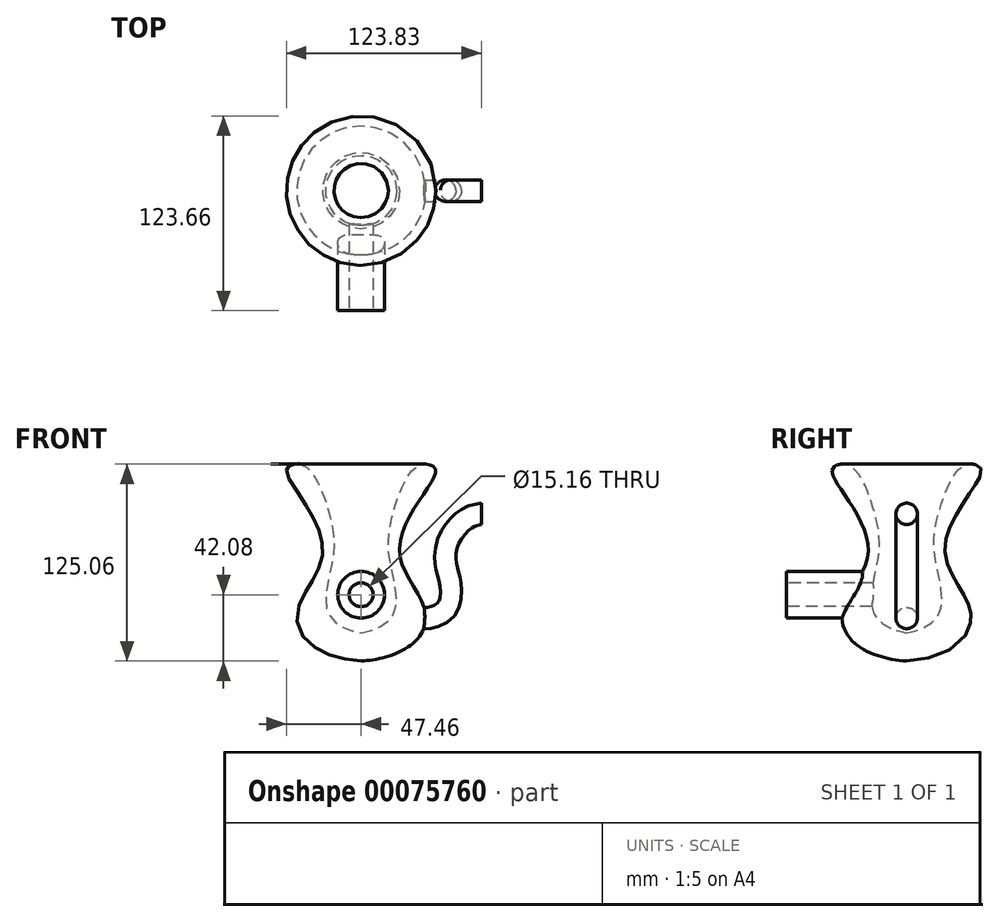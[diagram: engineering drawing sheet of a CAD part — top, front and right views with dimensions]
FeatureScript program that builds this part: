
annotation { "Feature Type Name" : "Feature", "Feature Type Description" : "" }
export const myFeature = defineFeature(function(context is Context, id is Id, definition is map)
    precondition{}
    {
        {
            var Q0;
            Q0=qCreatedBy(makeId("Front.planeOp"),FACE);
            var sketch = newSketch(context, id + "F0", { "sketchPlane" : qUnion([Q0])});
            skLineSegment(sketch, "E0", {"start": v(0, 92.1) * mm, "end": v(0, -59.81) * mm});
            skFitSpline(sketch, "E1", {"points": [v(0, -24.13) * mm, v(19.84, -13.55) * mm, v(21.5, 6.14) * mm, v(17.27, 30.67) * mm, v(19.81, 49.85) * mm, v(24.32, 64.23) * mm, v(36.45, 82) * mm, v(46.94, 80.49) * mm, v(41.13, 66.1) * mm, v(24.42, 26.34) * mm, v(40.37, -9.36) * mm, v(31.4, -32.1) * mm, v(0, -42.08) * mm, v(-7.08, -41.48) * mm, v(-6.29, -41.08) * mm, v(-12.27, -24.72) * mm], "startDerivative": vector(353.76, 54.94) * mm, "endDerivative": vector(-162.88, 343.94) * mm});
            skSolve(sketch);
        }
        {
            var Q0;
            {var subQ0=sQuery(id+"F0.wireOp",EDGE,"E1");Q0=makeQuery(id+"F0.imprint","IMPRINT",FACE,{"disambiguationData":[TD([[makeQuery(id+"F0.imprint","IMPRINT",EDGE,{"derivedFrom":subQ0}),-1.0]])]});}
            var Q1;
            Q1=sQuery(id+"F0.wireOp",EDGE,"E0");
            revolve(context, id + "F1", {"entities" : qUnion([Q0]), "axis" : qUnion([Q1]), "revolveType" : RevolveType.FULL});
        }
        {
            var Q0;
            Q0=qCreatedBy(makeId("Front.planeOp"),FACE);
            cPlane(context, id + "F2", {"entities" : qUnion([Q0]), "cplaneType" : CPlaneType.OFFSET, "offset" : 76.2 * mm, "width" : 152.4 * mm, "height" : 152.4 * mm});
        }
        {
            var Q0;
            Q0=qCreatedBy(id+"F2.planeOp",FACE);
            var sketch = newSketch(context, id + "F3", { "sketchPlane" : qUnion([Q0])});
            skCircle(sketch, "E2", {"center": v(0, 0) * mm, "radius": 14.85 * mm});
            skSolve(sketch);
        }
        {
            var Q0;
            Q0=makeQuery(id+"F3.imprint","IMPRINT",FACE,{"disambiguationData":[TD([[makeQuery(id+"F3.imprint","IMPRINT",EDGE,{"derivedFrom":sQuery(id+"F3.wireOp",EDGE,"E2")}),1.0]])]});
            var Q1;
            Q1=makeQuery(id+"F1.opRevolve","SWEPT_FACE",FACE,{"disambiguationData":[OSD([sQuery(id+"F0.wireOp",EDGE,"E1")])]});
            extrude(context, id + "F4", {"entities" : qUnion([Q0]), "operationType" : NewBodyOperationType.ADD, "endBound" : BoundingType.UP_TO_NEXT, "oppositeDirection" : true, "endBoundEntityFace" : qUnion([Q1]), "depth" : 25.4 * mm});
        }
        {
            var Q0;
            Q0=makeQuery(id+"F4.opExtrude","CAP_FACE",FACE,{"disambiguationData":[OSD([sQuery(id+"F3.wireOp",EDGE,"E2")])],"isStart":true});
            var sketch = newSketch(context, id + "F5", { "sketchPlane" : qUnion([Q0])});
            skCircle(sketch, "E3", {"center": v(0, 0) * mm, "radius": 7.58 * mm});
            skSolve(sketch);
        }
        {
            var Q0;
            Q0=makeQuery(id+"F5.imprint","IMPRINT",FACE,{"disambiguationData":[TD([[makeQuery(id+"F5.imprint","IMPRINT",EDGE,{"derivedFrom":sQuery(id+"F5.wireOp",EDGE,"E3")}),1.0]])]});
            extrude(context, id + "F6", {"entities" : qUnion([Q0]), "operationType" : NewBodyOperationType.REMOVE, "oppositeDirection" : true, "depth" : 73.26 * mm});
        }
        {
            var Q0;
            Q0=qCreatedBy(makeId("Right.planeOp"),FACE);
            cPlane(context, id + "F7", {"entities" : qUnion([Q0]), "cplaneType" : CPlaneType.OFFSET, "offset" : 76.2 * mm, "width" : 152.4 * mm, "height" : 152.4 * mm});
        }
        {
            var Q0;
            Q0=qCreatedBy(id+"F7.planeOp",FACE);
            var sketch = newSketch(context, id + "F8", { "sketchPlane" : qUnion([Q0])});
            skCircle(sketch, "E4", {"center": v(0, 51.38) * mm, "radius": 6.8 * mm});
            skSolve(sketch);
        }
        {
            var Q0;
            Q0=qCreatedBy(makeId("Front.planeOp"),FACE);
            var sketch = newSketch(context, id + "F9", { "sketchPlane" : qUnion([Q0])});
            skFitSpline(sketch, "E5", {"points": [v(76.37, 52.01) * mm, v(67.2, 49.18) * mm, v(54.7, 34.17) * mm, v(53.53, 17.66) * mm, v(56.03, 7.32) * mm, v(53.7, -8.68) * mm, v(40.85, -14.19) * mm, v(34.52, -14.02) * mm, v(33.68, -14.02) * mm, v(29.51, -12.19) * mm], "startDerivative": vector(-80.32, -11.9) * mm, "endDerivative": vector(-67.36, 33.23) * mm});
            skSolve(sketch);
        }
        {
            var Q0;
            Q0=makeQuery(id+"F8.imprint","IMPRINT",FACE,{"disambiguationData":[TD([[makeQuery(id+"F8.imprint","IMPRINT",EDGE,{"derivedFrom":sQuery(id+"F8.wireOp",EDGE,"E4")}),1.0]])]});
            var Q1;
            Q1=sQuery(id+"F9.wireOp",EDGE,"E5");
            sweep(context, id + "F10", {"operationType" : NewBodyOperationType.ADD, "profiles" : qUnion([Q0]), "path" : qUnion([Q1])});
        }
    });
